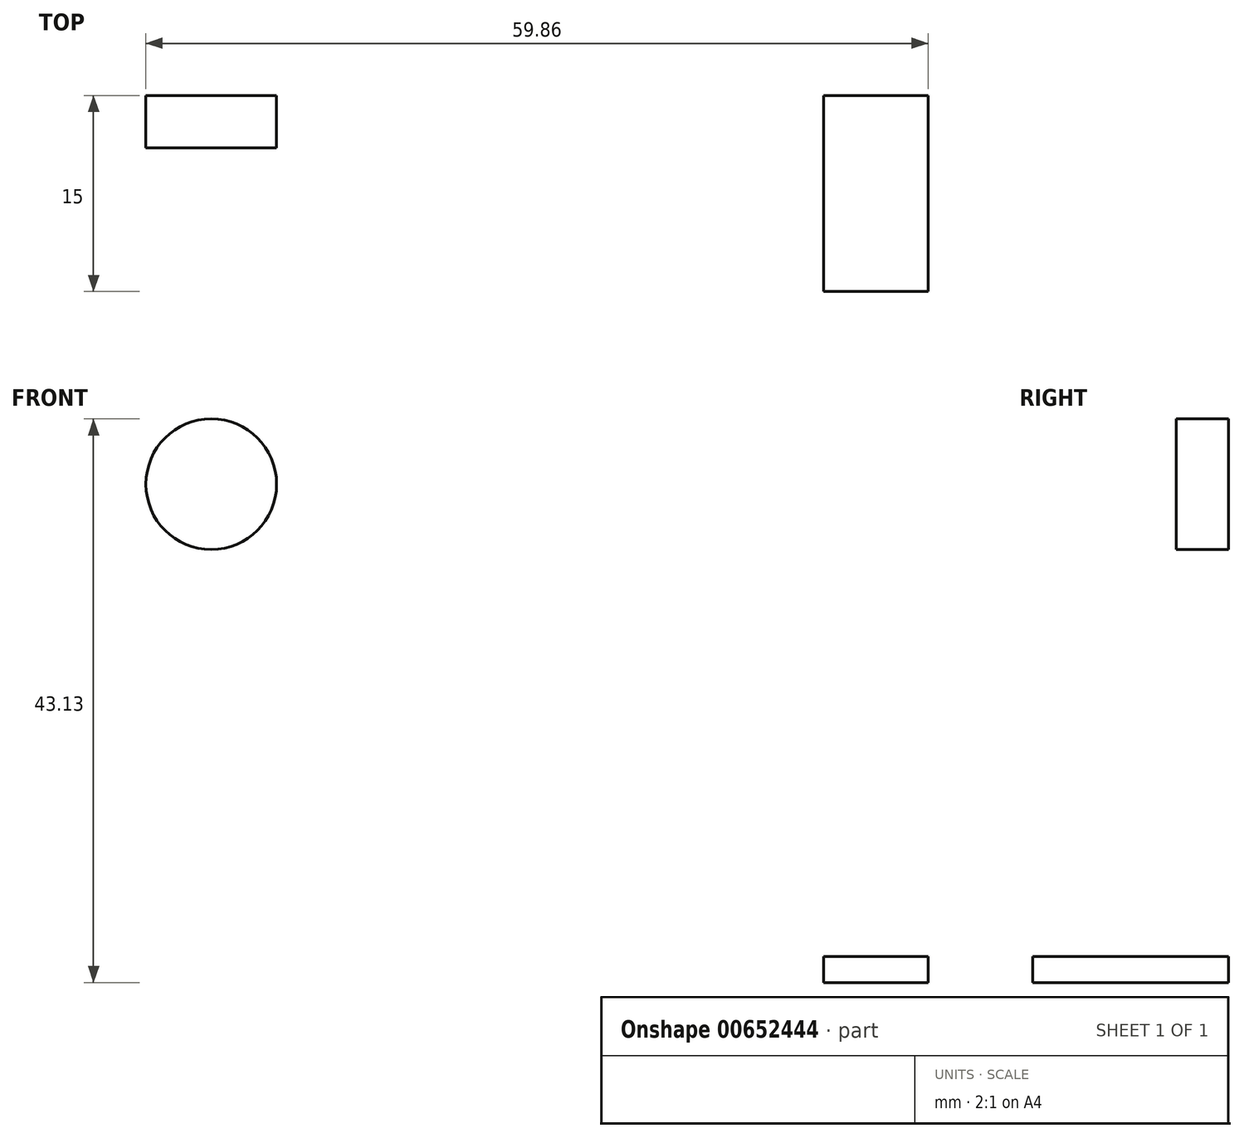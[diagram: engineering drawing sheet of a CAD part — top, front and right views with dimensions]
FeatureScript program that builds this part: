
annotation { "Feature Type Name" : "Feature", "Feature Type Description" : "" }
export const myFeature = defineFeature(function(context is Context, id is Id, definition is map)
    precondition{}
    {
        {
            var Q0;
            Q0=qCreatedBy(makeId("Front.planeOp"),FACE);
            var sketch = newSketch(context, id + "F0", { "sketchPlane" : qUnion([Q0])});
            skLineSegment(sketch, "E0.bottom", {"start": v(0, 0) * mm, "end": v(-8, 0) * mm});
            skLineSegment(sketch, "E0.top", {"start": v(0, 2) * mm, "end": v(-8, 2) * mm});
            skLineSegment(sketch, "E0.left", {"start": v(0, 0) * mm, "end": v(0, 2) * mm});
            skLineSegment(sketch, "E0.right", {"start": v(-8, 0) * mm, "end": v(-8, 2) * mm});
            skLineSegment(sketch, "E1.bottom", {"start": v(-4.69, 2) * mm, "end": v(-3.14, 2) * mm});
            skLineSegment(sketch, "E1.top", {"start": v(-4.69, 2.6) * mm, "end": v(-3.14, 2.6) * mm});
            skLineSegment(sketch, "E1.left", {"start": v(-4.69, 2) * mm, "end": v(-4.69, 2.6) * mm});
            skLineSegment(sketch, "E1.right", {"start": v(-3.14, 2) * mm, "end": v(-3.14, 2.6) * mm});
            skSolve(sketch);
        }
        {
            var Q0;
            Q0=makeQuery(id+"F0.imprint","IMPRINT",FACE,{"disambiguationData":[TD([[makeQuery(id+"F0.imprint","IMPRINT",EDGE,{"derivedFrom":sQuery(id+"F0.wireOp",EDGE,"E0.bottom")}),-1.0]])]});
            var Q1;
            Q1=makeQuery(id+"F0.imprint","IMPRINT",FACE,{"disambiguationData":[TD([[makeQuery(id+"F0.imprint","IMPRINT",EDGE,{"derivedFrom":sQuery(id+"F0.wireOp",EDGE,"E1.bottom")}),1.0]])]});
            extrude(context, id + "F1", {"entities" : qUnion([Q0, Q1]), "depth" : 15 * mm, "offsetDistance" : 25 * mm});
        }
        {
            var Q0;
            Q0=qCreatedBy(makeId("Front.planeOp"),FACE);
            var sketch = newSketch(context, id + "F2", { "sketchPlane" : qUnion([Q0])});
            skCircle(sketch, "E2", {"center": v(-54.86, 38.13) * mm, "radius": 5 * mm});
            skSolve(sketch);
        }
        {
            var Q0;
            Q0 = qSketchRegion(id + "F2", true);
            extrude(context, id + "F3", {"entities" : qUnion([Q0]), "depth" : 4 * mm, "offsetDistance" : 25 * mm});
        }
    });
